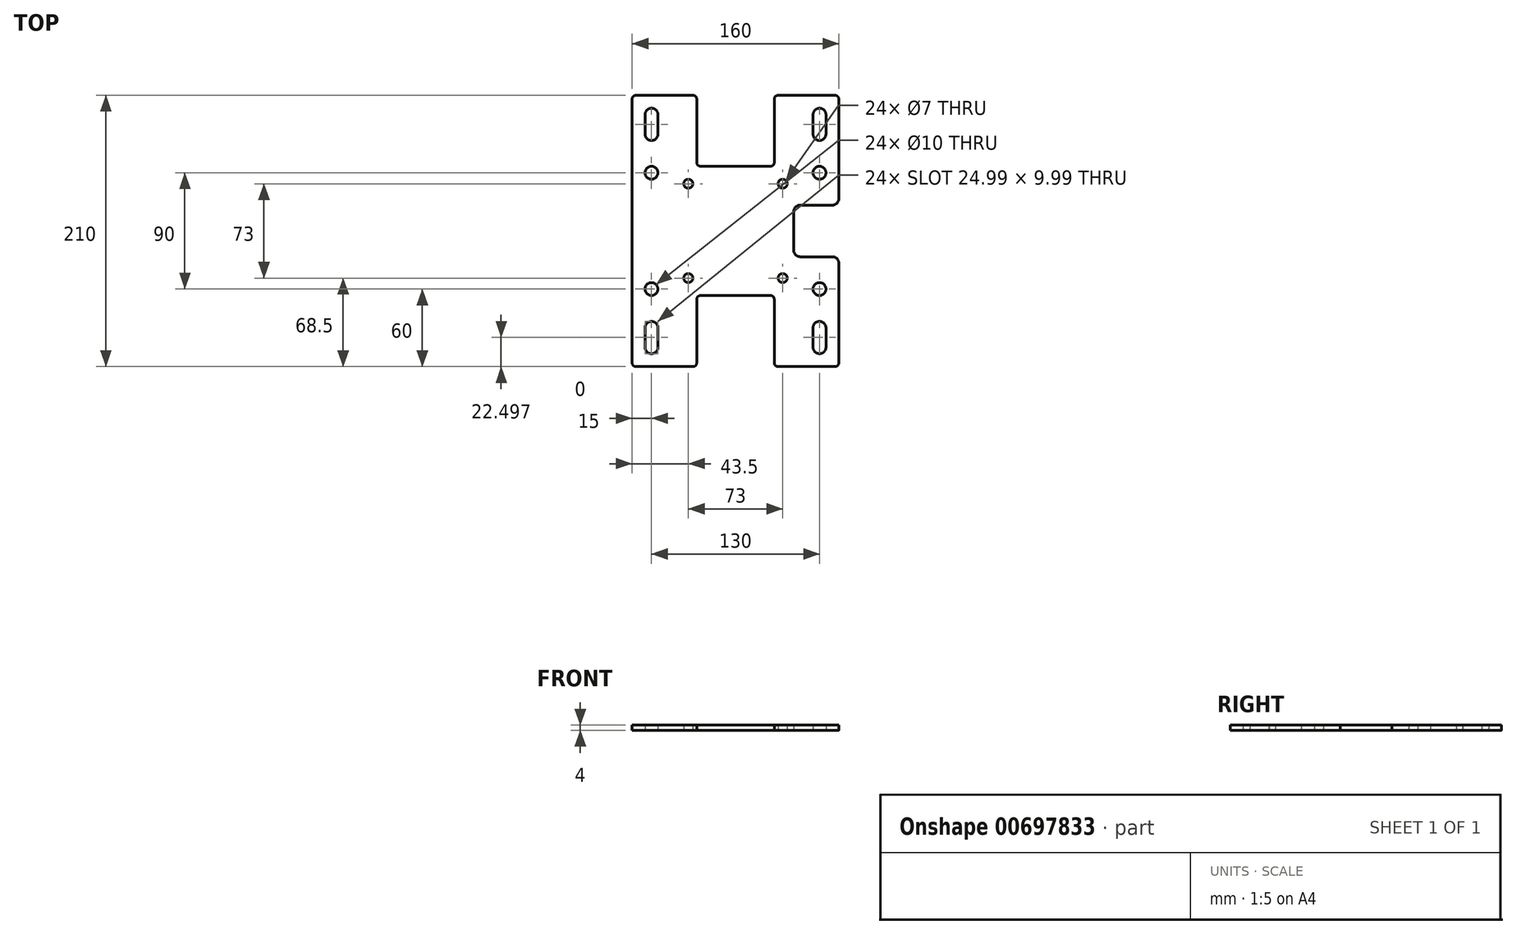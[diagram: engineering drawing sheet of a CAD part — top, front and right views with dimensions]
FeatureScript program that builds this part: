
annotation { "Feature Type Name" : "Feature", "Feature Type Description" : "" }
export const myFeature = defineFeature(function(context is Context, id is Id, definition is map)
    precondition{}
    {
        {
            var Q0;
            Q0=qCreatedBy(makeId("Top.planeOp"),FACE);
            var sketch = newSketch(context, id + "F0", { "sketchPlane" : qUnion([Q0])});
            skLineSegment(sketch, "E0.bottom", {"start": v(-77, -105) * mm, "end": v(-33, -105) * mm});
            skLineSegment(sketch, "E0.top", {"start": v(-77, 105) * mm, "end": v(-33, 105) * mm});
            skLineSegment(sketch, "E0.left", {"start": v(-80, -102) * mm, "end": v(-80, 102) * mm});
            skLineSegment(sketch, "E0.right", {"start": v(80, -102) * mm, "end": v(80, -20) * mm});
            skPoint(sketch, "E0.middle", {"position": v(0, 0) * mm});
            skLineSegment(sketch, "E1", {"start": v(-30, 102) * mm, "end": v(-30, 53) * mm});
            skLineSegment(sketch, "E2", {"start": v(-27, 50) * mm, "end": v(27, 50) * mm});
            skLineSegment(sketch, "E3", {"start": v(30, 53) * mm, "end": v(30, 102) * mm});
            skLineSegment(sketch, "E4", {"start": v(-30, -53) * mm, "end": v(-30, -102) * mm});
            skLineSegment(sketch, "E5", {"start": v(-27, -50) * mm, "end": v(27, -50) * mm});
            skLineSegment(sketch, "E6", {"start": v(30, -53) * mm, "end": v(30, -102) * mm});
            skLineSegment(sketch, "E7.trimOffspring", {"start": v(33, 105) * mm, "end": v(77, 105) * mm});
            skLineSegment(sketch, "E8.trimOffspring", {"start": v(33, -105) * mm, "end": v(77, -105) * mm});
            skCircle(sketch, "E9", {"center": v(-36.5, 36.5) * mm, "radius": 3.5 * mm});
            skCircle(sketch, "E10", {"center": v(-36.5, -36.5) * mm, "radius": 3.5 * mm});
            skCircle(sketch, "E11", {"center": v(36.5, -36.5) * mm, "radius": 3.5 * mm});
            skCircle(sketch, "E12", {"center": v(36.5, 36.5) * mm, "radius": 3.5 * mm});
            skArc(sketch, "E13", {"start": v(-60, 89.77) * mm, "mid": v(-65, 95) * mm, "end": v(-70, 89.77) * mm});
            skArc(sketch, "E14", {"start": v(-70, 75.23) * mm, "mid": v(-65.23, 70) * mm, "end": v(-60, 74.77) * mm});
            skCircle(sketch, "E15", {"center": v(-65, 45) * mm, "radius": 5 * mm});
            skLineSegment(sketch, "E16", {"start": v(-70, 90.23) * mm, "end": v(-70, 74.77) * mm});
            skLineSegment(sketch, "E17", {"start": v(-60, 74.77) * mm, "end": v(-60, 89.77) * mm});
            skCircle(sketch, "E18.MirrorC", {"center": v(-65, -45) * mm, "radius": 5 * mm});
            skArc(sketch, "E19.MirrorCS", {"start": v(-70, -75.23) * mm, "mid": v(-65.23, -70) * mm, "end": v(-60, -74.77) * mm});
            skLineSegment(sketch, "E20.MirrorCS", {"start": v(-60, -74.77) * mm, "end": v(-60, -89.77) * mm});
            skArc(sketch, "E21.MirrorCS", {"start": v(-60, -89.77) * mm, "mid": v(-65, -95) * mm, "end": v(-70, -89.77) * mm});
            skLineSegment(sketch, "E22.MirrorCS", {"start": v(-70, -90.23) * mm, "end": v(-70, -74.77) * mm});
            skCircle(sketch, "E23.MirrorC", {"center": v(65, 45) * mm, "radius": 5 * mm});
            skCircle(sketch, "E24.MirrorC", {"center": v(65, -45) * mm, "radius": 5 * mm});
            skArc(sketch, "E25.MirrorCS", {"start": v(70, -75.23) * mm, "mid": v(65.23, -70) * mm, "end": v(60, -74.77) * mm});
            skLineSegment(sketch, "E26.MirrorCS", {"start": v(60, -74.77) * mm, "end": v(60, -89.77) * mm});
            skLineSegment(sketch, "E27.MirrorCS", {"start": v(70, -90.23) * mm, "end": v(70, -74.77) * mm});
            skArc(sketch, "E28.MirrorCS", {"start": v(60, -89.77) * mm, "mid": v(65, -95) * mm, "end": v(70, -89.77) * mm});
            skArc(sketch, "E29.MirrorCS", {"start": v(70, 75.23) * mm, "mid": v(65.23, 70) * mm, "end": v(60, 74.77) * mm});
            skLineSegment(sketch, "E30.MirrorCS", {"start": v(60, 74.77) * mm, "end": v(60, 89.77) * mm});
            skArc(sketch, "E31.MirrorCS", {"start": v(60, 89.77) * mm, "mid": v(65, 95) * mm, "end": v(70, 89.77) * mm});
            skLineSegment(sketch, "E32.MirrorCS", {"start": v(70, 90.23) * mm, "end": v(70, 74.77) * mm});
            skPoint(sketch, "E33.visualSharp", {"position": v(-30, 50) * mm});
            skArc(sketch, "E33.filletArc", {"start": v(-30, 53) * mm, "mid": v(-29.12, 50.88) * mm, "end": v(-27, 50) * mm});
            skPoint(sketch, "E34.visualSharp", {"position": v(30, 50) * mm});
            skArc(sketch, "E34.filletArc", {"start": v(27, 50) * mm, "mid": v(29.12, 50.88) * mm, "end": v(30, 53) * mm});
            skPoint(sketch, "E35.visualSharp", {"position": v(30, 105) * mm});
            skArc(sketch, "E35.filletArc", {"start": v(33, 105) * mm, "mid": v(30.88, 104.12) * mm, "end": v(30, 102) * mm});
            skPoint(sketch, "E36.visualSharp", {"position": v(80, 105) * mm});
            skArc(sketch, "E36.filletArc", {"start": v(80, 102) * mm, "mid": v(79.12, 104.12) * mm, "end": v(77, 105) * mm});
            skPoint(sketch, "E37.visualSharp", {"position": v(80, -105) * mm});
            skArc(sketch, "E37.filletArc", {"start": v(77, -105) * mm, "mid": v(79.12, -104.12) * mm, "end": v(80, -102) * mm});
            skPoint(sketch, "E38.visualSharp", {"position": v(30, -105) * mm});
            skArc(sketch, "E38.filletArc", {"start": v(30, -102) * mm, "mid": v(30.88, -104.12) * mm, "end": v(33, -105) * mm});
            skPoint(sketch, "E39.visualSharp", {"position": v(30, -50) * mm});
            skArc(sketch, "E39.filletArc", {"start": v(30, -53) * mm, "mid": v(29.12, -50.88) * mm, "end": v(27, -50) * mm});
            skPoint(sketch, "E40.visualSharp", {"position": v(-30, -50) * mm});
            skArc(sketch, "E40.filletArc", {"start": v(-27, -50) * mm, "mid": v(-29.12, -50.88) * mm, "end": v(-30, -53) * mm});
            skPoint(sketch, "E41.visualSharp", {"position": v(-30, -105) * mm});
            skArc(sketch, "E41.filletArc", {"start": v(-33, -105) * mm, "mid": v(-30.88, -104.12) * mm, "end": v(-30, -102) * mm});
            skPoint(sketch, "E42.visualSharp", {"position": v(-80, -105) * mm});
            skArc(sketch, "E42.filletArc", {"start": v(-80, -102) * mm, "mid": v(-79.12, -104.12) * mm, "end": v(-77, -105) * mm});
            skPoint(sketch, "E43.visualSharp", {"position": v(-30, 105) * mm});
            skArc(sketch, "E43.filletArc", {"start": v(-30, 102) * mm, "mid": v(-30.88, 104.12) * mm, "end": v(-33, 105) * mm});
            skPoint(sketch, "E44.visualSharp", {"position": v(-80, 105) * mm});
            skArc(sketch, "E44.filletArc", {"start": v(-77, 105) * mm, "mid": v(-79.12, 104.12) * mm, "end": v(-80, 102) * mm});
            skLineSegment(sketch, "E45.bottom", {"start": v(45, 20) * mm, "end": v(80, 20) * mm});
            skLineSegment(sketch, "E45.top", {"start": v(45, -20) * mm, "end": v(80, -20) * mm});
            skLineSegment(sketch, "E45.left", {"start": v(45, 20) * mm, "end": v(45, -20) * mm});
            skPoint(sketch, "E45.middle", {"position": v(80, 0) * mm});
            skLineSegment(sketch, "E46.trimOffspring", {"start": v(80, 20) * mm, "end": v(80, 102) * mm});
            skPoint(sketch, "E45.right.end.orphan", {"position": v(115, -20) * mm});
            skPoint(sketch, "E45.right.start.orphan", {"position": v(115, 20) * mm});
            skSolve(sketch);
        }
        {
            var Q0;
            Q0 = qSketchRegion(id + "F0", true);
            extrude(context, id + "F1", {"entities" : qUnion([Q0]), "depth" : 4 * mm, "offsetDistance" : 25 * mm});
        }
        {
            var Q0;
            Q0=makeQuery(id+"F1.opExtrude","SWEPT_EDGE",EDGE,{"disambiguationData":[OSD([sQuery(id+"F0.wireOp",EDGE,"E0.right"),sQuery(id+"F0.wireOp",EDGE,"E45.top")])]});
            var Q1;
            Q1=makeQuery(id+"F1.opExtrude","SWEPT_EDGE",EDGE,{"disambiguationData":[OSD([sQuery(id+"F0.wireOp",EDGE,"E45.top"),sQuery(id+"F0.wireOp",EDGE,"E45.left")])]});
            var Q2;
            Q2=makeQuery(id+"F1.opExtrude","SWEPT_EDGE",EDGE,{"disambiguationData":[OSD([sQuery(id+"F0.wireOp",EDGE,"E45.bottom"),sQuery(id+"F0.wireOp",EDGE,"E45.left")])]});
            var Q3;
            Q3=makeQuery(id+"F1.opExtrude","SWEPT_EDGE",EDGE,{"disambiguationData":[OSD([sQuery(id+"F0.wireOp",EDGE,"E45.bottom"),sQuery(id+"F0.wireOp",EDGE,"E46.trimOffspring")])]});
            fillet(context, id + "F2", {"entities" : qUnion([Q0, Q1, Q2, Q3]), "tangentPropagation" : true, "radius" : 5 * mm, "defaultsChanged" : false, "vertexSettings" : [], "allowEdgeOverflow" : false});
        }
    });
